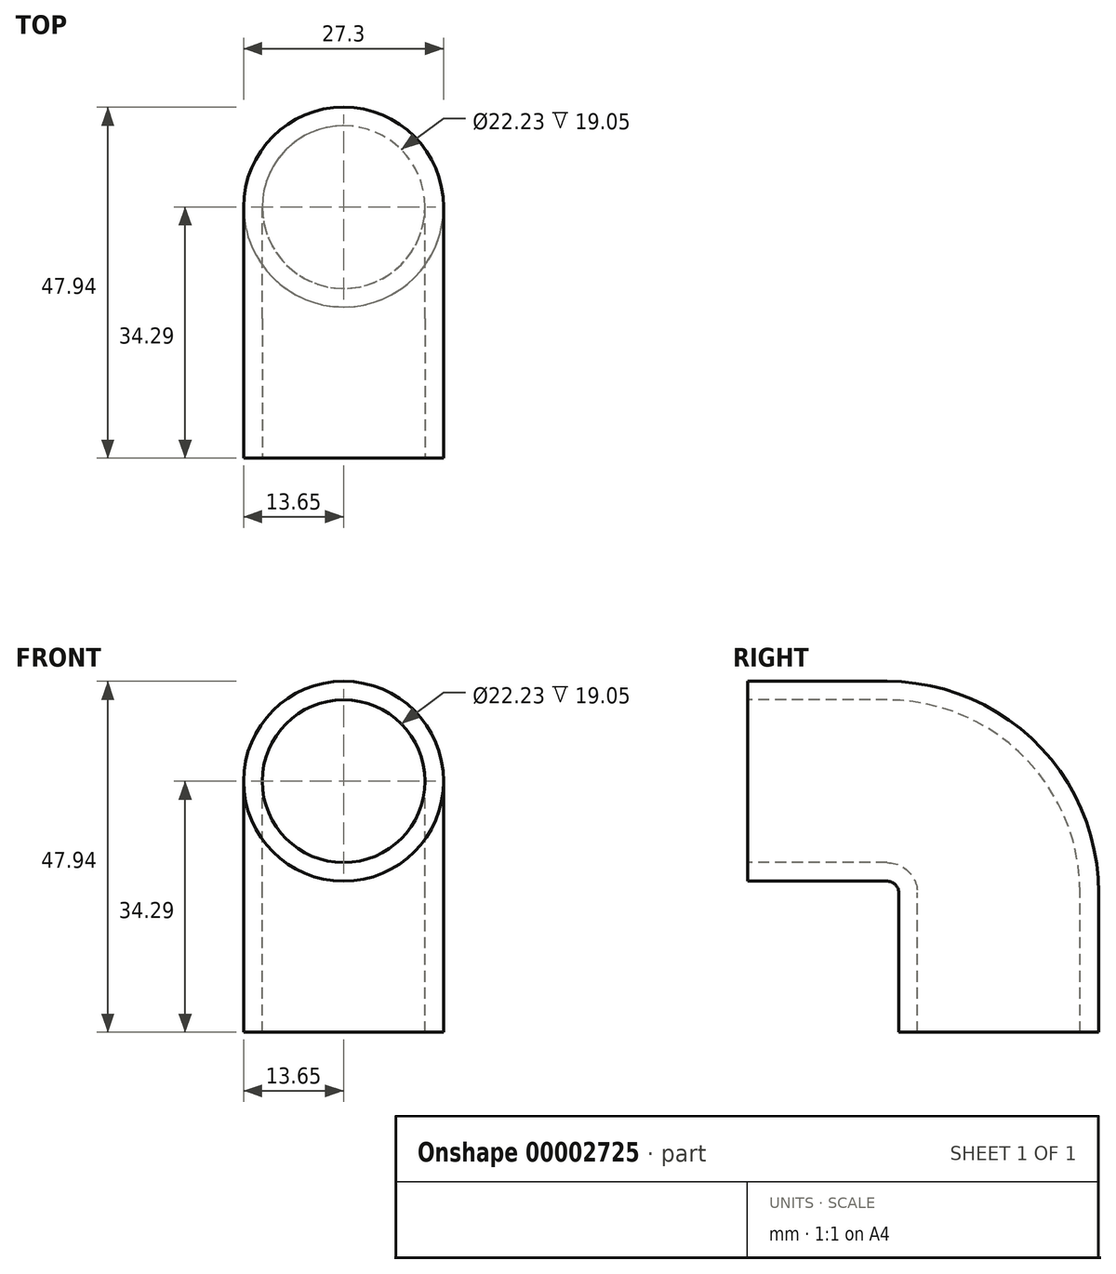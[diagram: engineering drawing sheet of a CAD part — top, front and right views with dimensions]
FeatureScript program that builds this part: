
annotation { "Feature Type Name" : "Feature", "Feature Type Description" : "" }
export const myFeature = defineFeature(function(context is Context, id is Id, definition is map)
    precondition{}
    {
        {
            var Q0;
            Q0=qCreatedBy(makeId("Right.planeOp"),FACE);
            var sketch = newSketch(context, id + "F0", { "sketchPlane" : qUnion([Q0])});
            skLineSegment(sketch, "E0", {"start": v(0, 0) * mm, "end": v(0, 19.05) * mm});
            skLineSegment(sketch, "E1", {"start": v(-15.24, 34.3) * mm, "end": v(-34.3, 34.3) * mm});
            skPoint(sketch, "E2.visualSharp", {"position": v(0, 34.3) * mm});
            skArc(sketch, "E2.filletArc", {"start": v(0, 19.05) * mm, "mid": v(-4.46, 29.83) * mm, "end": v(-15.24, 34.3) * mm});
            skSolve(sketch);
        }
        {
            var Q0;
            Q0=qCreatedBy(makeId("Top.planeOp"),FACE);
            var sketch = newSketch(context, id + "F1", { "sketchPlane" : qUnion([Q0])});
            skCircle(sketch, "E3", {"center": v(0, 0) * mm, "radius": 13.65 * mm});
            skSolve(sketch);
        }
        {
            var Q0;
            Q0=makeQuery(id+"F1.imprint","IMPRINT",FACE,{"disambiguationData":[TD([[makeQuery(id+"F1.imprint","IMPRINT",EDGE,{"derivedFrom":sQuery(id+"F1.wireOp",EDGE,"E3")}),1.0]])]});
            var Q1;
            Q1=sQuery(id+"F0.wireOp",EDGE,"E0");
            var Q2;
            Q2=sQuery(id+"F0.wireOp",EDGE,"E2.filletArc");
            var Q3;
            Q3=sQuery(id+"F0.wireOp",EDGE,"E1");
            sweep(context, id + "F2", {"profiles" : qUnion([Q0]), "path" : qUnion([Q1, Q2, Q3])});
        }
        {
            var Q0;
            Q0=makeQuery(id+"F2.opSweep","CAP_FACE",FACE,{"disambiguationData":[OSD([sQuery(id+"F0.wireOp",VERTEX,"E1.end"),sQuery(id+"F1.wireOp",EDGE,"E3")])],"isStart":false});
            var Q1;
            Q1=makeQuery(id+"F2.opSweep","CAP_FACE",FACE,{"disambiguationData":[OSD([sQuery(id+"F0.wireOp",VERTEX,"E0.start"),sQuery(id+"F1.wireOp",EDGE,"E3")])],"isStart":true});
            shell(context, id + "F3", {"entities" : qUnion([Q0, Q1]), "thickness" : 2.54 * mm});
        }
    });
